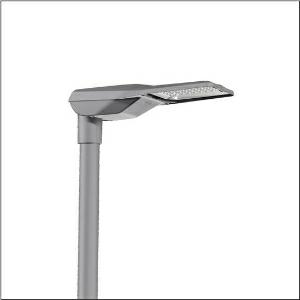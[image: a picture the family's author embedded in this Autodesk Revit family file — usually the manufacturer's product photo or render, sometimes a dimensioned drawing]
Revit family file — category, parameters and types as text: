
# Revit family: streetlight_sl_21_iq_mini___st1_5a_5xe2p31d08hb_3c75
name_source: partatom
category: Lighting Fixtures
units: mm (PartAtom-declared; Revit-internal decimal feet)

## family parameters
Cut with Voids When Loaded = No
Host = Face
Light Source = No
Part Type = Normal
Room Calculation Point = No
Round Connector Dimension = Use Diameter
Shared = No

## types (1)
- --- (1 x LED, 9290 lm, 70.9 W, 3000K)
    Apparent Load = 71 VA
    CIE Flux Codes = 22 53 95 100 100
    Color Rendering = 70
    Color Temperature = 3000K
    Default Elevation = 1800 mm
    Description = Streetlight SL 21 iQ mini, mast luminaire, primary light control with lens, of PMMA, primary optical cover: cover, of toughened safety glass, transparent, light distribution: ST1.5a, light emission: direct distribution, primary light characteristic: asymmetric, installation type: post-top, side-entry, LED, High Power LED, rated luminous flux: 9.290lm, luminous efficacy: 131lm/W, light colour: 730, colour temperature: 3000K, control gear: iQ-Comfort, control: Auto-Match, Temp-Guard, Lumen-Switch, Night-Set, Smart-Wire, Light-Fading, Desk-Remote (wireless, voltage-free reading and setting of iQ features in the workshop via application-optimized NFC function/RFID function), optimised constant luminous flux control (CLO 2.0), pre-setting: linear dimming characteristic, mains connection: 220..240V, AC, 50/60Hz, start of lifetime: 71W, end of service life: 75W, reduction: 31W, luminaire housing, of diecast aluminium, powder-coated, Siteco® metallic grey (DB 702S), corrosivity category C5 mid according to DIN EN ISO 12944, please order mast flange separately, inclination adjustable: 0°, 5°, 10°, 15°, sealing non-destructively replaceable, multi-level sealing system, length: 628mm, width: 235mm, height: 110mm, mast flange for spigot size: 42mm (side-entry): 5XC10008XM4, 60/48mm (side-entry/post-top): 5XC10108XM2, 76/60mm (side-entry/post-top): 5XC10108XM1, mounting height: 4..8m, protection rating (complete): IP66, insulation class (complete): insulation class II (safety insulation), certification: CE, ENEC, ENEC+, VDE, impact resistance: IK10, permissible operating ambient temperature for outdoor applications: -40..+50°C, standard-compliant lighting for roads and squares, packaging unit: 1 piece

Light Distribution: ST1.5a
    Height = 110 mm
    Lamp = 1 x LED
    Lamp Light Flux = 9290 lm
    Lamp Power = 70.9 W
    Lamp count = 1
    Length = 625 mm
    Luminous efficacy = 131 lm/W
    Manufacturer = Siteco
    ModVariant = No
    Model = 5XE2P31D08HB
    Number of Poles = 1
    OnlyDefault = Yes
    Power Factor = 1
    Product Name = Streetlight SL 21 iQ mini | ST1.5a
    Product group = mast luminaire | pylon top
    ProductGroupID = 6100
    Protection Class = Protection class II
    Protection Degree = IP 66
    RLX_Detail_Level = 1
    RLX_Emergency_Light_Flux = 0 lm
    RLX_Emergency_Type = 0
    RLX_Emergency_Type_DB = No
    RlxData = <blob elided: 29941 chars, md5=b7297d04>
    Socket = socket
    Standby Power = 0 W
    System Light Flux = 9290 lm
    System Power = 71 W
    Type Comments = factory setting: luminous flux: 100 % | dim-lin: 254 | 711 mA
    Type Image = l_1003519.jpg
    URL = http://relux.com
    VarID = @adj_178565
    Voltage = 0 V
    Weight = 0.00 kg
    Width = 234 mm

## geometry (parser evidence)
native form markers: Blend x4, Sweep x7
no freeform markers — native parametric forms only
